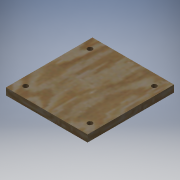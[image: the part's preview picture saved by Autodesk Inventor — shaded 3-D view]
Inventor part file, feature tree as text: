
AUTODESK INVENTOR PART (.ipt)
format: ipt  version: 2017 (Build 210142000, 142)  size: 130,048 bytes
history: native  units: in
note: dims shown in document units (in); Inventor stores cm internally (conversion verified against a paired STEP export)
features: sketch x3, plane x2, extrude x1, hole x1
ambient origin geometry x8: Origin, YZ Plane, XZ Plane, XY Plane, X Axis, Y Axis, Z Axis, Center Point
bodies: Solid1 (feature_tree)
feature tree (7):
  plane  "Work Plane1"
  sketch  "Sketch3"  dims[d13=8.25in d14=8.75in]
  plane  "Work Plane2"
  extrude  "Extrusion2"  Depth=8.75in
  hole  "Hole2"  [1 undecoded]
  sketch  "Sketch4"  dims[d15=8.25in d16=8.75in d17=0.7in d18=0.0in]
  sketch  "Sketch6"  dims[d33=0.5in d34=0.5in d35=0.5in d36=0.5in d37=0.5in d38=0.75in d39=0.375in d40=0.25in d41=0.5635in d42=1.0in d43=0.8108in]
note: 1 required parameter value undecoded (feature->parameter linkage not recoverable at this tier; creation-order binding heuristic only, values carry confidence <= 0.55)
